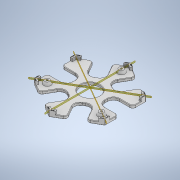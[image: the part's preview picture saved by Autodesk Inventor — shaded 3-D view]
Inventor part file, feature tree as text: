
AUTODESK INVENTOR PART (.ipt)
format: ipt  version: 2020 (Build 240168000, 168)  size: 1,028,096 bytes
history: native  units: in
note: dims shown in document units (in); Inventor stores cm internally (conversion verified against a paired STEP export)
features: plane x14, sketch x12, fillet x10, extrude x6, pattern_circular x5, hole x2, emboss x1, loft x1, mirror x1
ambient origin geometry x8: Origin, YZ Plane, XZ Plane, XY Plane, X Axis, Y Axis, Z Axis, Center Point
bodies: Solid1 (feature_tree)
feature tree (52):
  extrude  "Extrusion1"  Depth=3.3465in
  extrude  "Extrusion2"  TaperAngle=0.0deg  [1 undecoded]
  extrude  "Extrusion4"  Depth=0.2362in TaperAngle=0.0deg
  pattern_circular  "Circular Pattern2"  Count=6 Angle=360.0deg
  plane  "Work Plane1"
  extrude  "Extrusion6"  TaperAngle=0.0deg  [1 undecoded]
  emboss  "Emboss1"
  extrude  "Extrusion7"  Depth=0.2362in
  pattern_circular  "Circular Pattern5"  Count=4  [1 undecoded]
  fillet  "Fillet6"  Radius=0.2362in
  fillet  "Fillet7"  Radius=0.9843in
  fillet  "Fillet9"  Radius=0.9843in
  fillet  "Fillet10"  Radius=2.2047in
  fillet  "Fillet11"  Radius=1.378in
  sketch  "Sketch12"  dims[d37=0.0in]
  plane  "Work Plane3"
  loft  "Loft1"
  fillet  "Fillet12"  Radius=1.5748in
  hole  "Hole3"  [1 undecoded]
  hole  "Hole4"  [1 undecoded]
  pattern_circular  "Circular Pattern8"  [2 undecoded]
  extrude  "Extrusion9"  Depth=0.0394in
  plane  "Work Plane4"
  mirror  "Mirror2"
  pattern_circular  "Circular Pattern9"  [2 undecoded]
  fillet  "Fillet13"  Radius=0.0394in
  fillet  "Fillet14"  Radius=2.5591in
  fillet  "Fillet15"  Radius=0.5906in
  fillet  "Fillet16"  Radius=2.5591in
  pattern_circular  "Circular Pattern10"  [2 undecoded]
  sketch  "Sketch1"  dims[d1=0.0in d2=3.3465in]
  sketch  "Sketch2"  dims[d3=0.4724in d4=0.0in d5=0.0in]
  sketch  "Sketch6"  dims[d6=3.1496in d7=0.2362in d8=0.0in]
  sketch  "Sketch9"  dims[d34=0.0in]
  sketch  "Sketch10"  dims[d35=0.3937in]
  sketch  "Sketch11"  dims[d36=0.3937in]
  sketch  "Sketch13"  dims[d38=0.4331in d39=0.0in d40=2.3622in d41=360.0deg]
  sketch  "Sketch15"  dims[d52=1.2795in d64=0.0in]
  sketch  "Sketch16"  dims[d65=0.5906in d67=0.5906in d68=1.5748in d69=0.2362in d70=0.0in d71=0.9843in d72=0.9843in d76=2.2047in d77=1.378in]
  sketch  "Sketch17"  dims[d78=2.2835in d79=0.0079in d80=0.0in d81=1.5748in]
  sketch  "Sketch19"  dims[d82=0.2362in d83=0.0in d85=2.3622in d86=360.0deg d88=0.2362in d89=0.0394in d91=0.0394in d92=0.0394in d93=0.0394in d94=2.5591in d95=0.5906in d101=2.5591in d102=0.0in d103=0.3937in d104=0.0in d106=0.0in d107=90.0deg d108=0.0in d109=90.0deg d110=0.0in d111=90.0deg d115=0.0394in d116=0.1575in d117=0.2362in d118=0.1575in d119=0.0787in d120=90.0deg d121=3.937in d122=0.0in d123=0.315in d124=0.2362in d125=0.1575in d126=0.0787in d127=90.0deg d128=0.315in d129=0.8108in d130=1.1811in d131=360.0deg d135=0.0197in d136=0.0197in d137=0.0906in d138=0.1969in d139=0.0in d140=0.0in d141=0.0472in d142=0.0472in d143=0.2559in d144=0.0in d145=2.3622in d146=360.0deg d148=0.0394in d149=0.0394in d150=0.0098in d151=0.0098in d152=2.3622in d153=360.0deg]
  plane  "Work Plane5"
  plane  "Work Plane6"
  plane  "Work Plane7"
  plane  "Work Plane8"
  plane  "Work Plane9"
  plane  "Work Plane10"
  plane  "Work Plane11"
  plane  "Work Plane12"
  plane  "Work Plane13"
  plane  "Work Plane14"
  plane  "Work Plane15"
note: 11 required parameter values undecoded (feature->parameter linkage not recoverable at this tier; creation-order binding heuristic only, values carry confidence <= 0.55)
